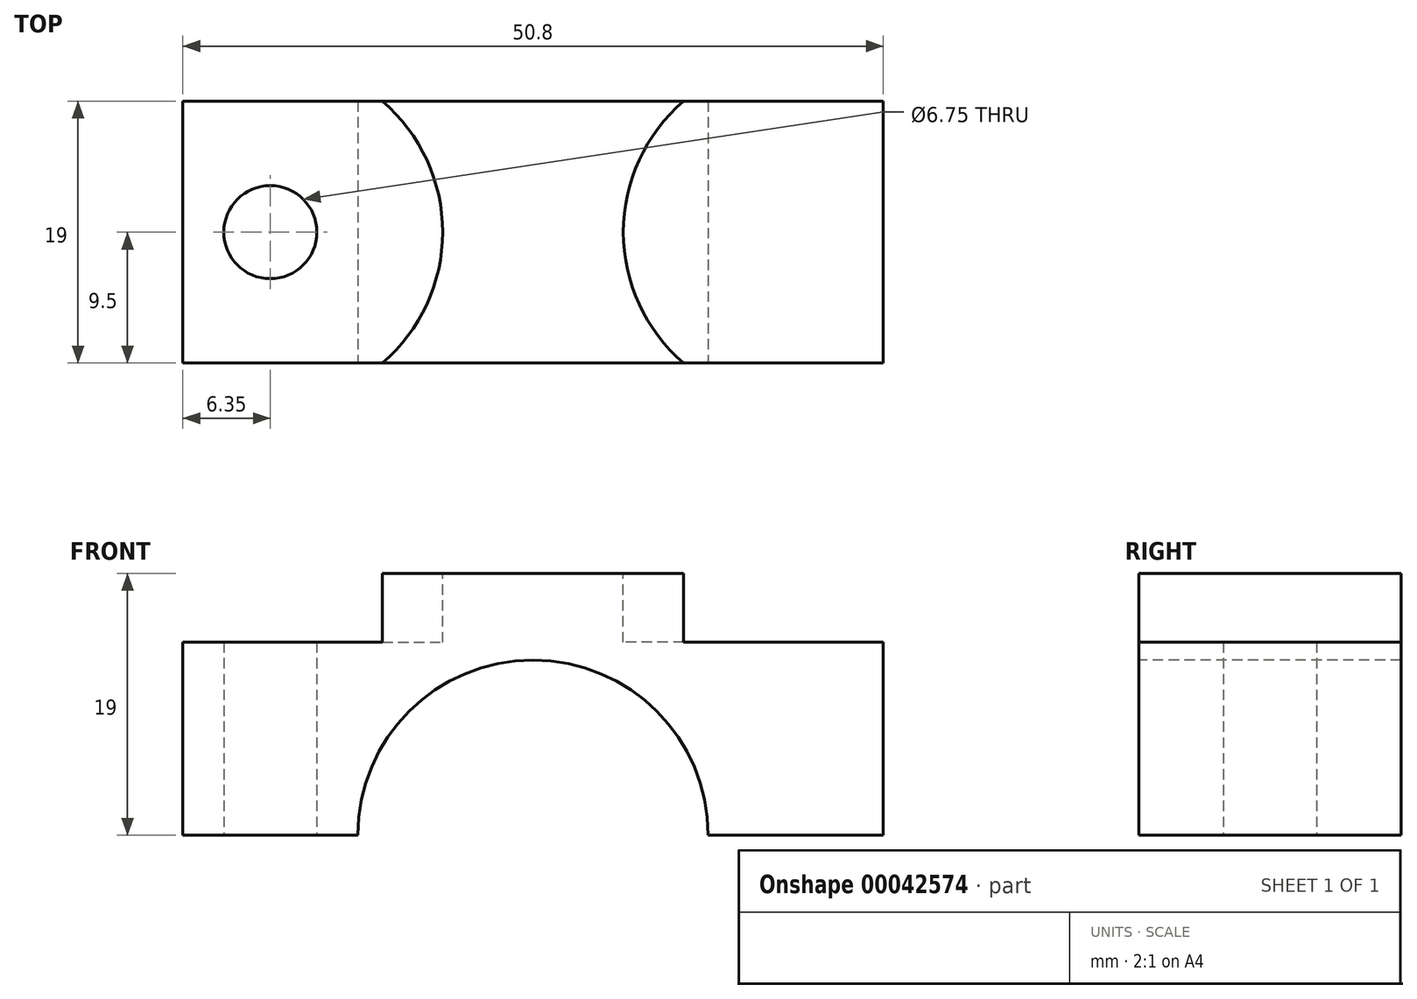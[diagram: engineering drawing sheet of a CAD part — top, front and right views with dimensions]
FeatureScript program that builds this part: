
annotation { "Feature Type Name" : "Feature", "Feature Type Description" : "" }
export const myFeature = defineFeature(function(context is Context, id is Id, definition is map)
    precondition{}
    {
        {
            var Q0;
            Q0=qCreatedBy(makeId("Front.planeOp"),FACE);
            var sketch = newSketch(context, id + "F0", { "sketchPlane" : qUnion([Q0])});
            skCircle(sketch, "E0", {"center": v(0, 0) * mm, "radius": 12.7 * mm});
            skLineSegment(sketch, "E1", {"start": v(0, 0) * mm, "end": v(25.4, 0) * mm});
            skLineSegment(sketch, "E2", {"start": v(25.4, 0) * mm, "end": v(25.4, 19) * mm});
            skLineSegment(sketch, "E3", {"start": v(25.4, 19) * mm, "end": v(-25.4, 19) * mm});
            skLineSegment(sketch, "E4", {"start": v(-25.4, 19) * mm, "end": v(-25.4, 0) * mm});
            skLineSegment(sketch, "E5", {"start": v(-25.4, 0) * mm, "end": v(0, 0) * mm});
            skSolve(sketch);
        }
        {
            var Q0;
            {var subQ6=sQuery(id+"F0.wireOp",EDGE,"E2");Q0=makeQuery(id+"F0.imprint","IMPRINT",FACE,{"disambiguationData":[TD([[makeQuery(id+"F0.imprint","IMPRINT",EDGE,{"derivedFrom":subQ6}),1.0]])]});}
            extrude(context, id + "F1", {"entities" : qUnion([Q0]), "oppositeDirection" : true, "depth" : 19 * mm});
        }
        {
            var Q0;
            Q0=makeQuery(id+"F1.opExtrude","SWEPT_FACE",FACE,{"disambiguationData":[OSD([sQuery(id+"F0.wireOp",EDGE,"E5")])]});
            var sketch = newSketch(context, id + "F2", { "sketchPlane" : qUnion([Q0])});
            skLineSegment(sketch, "E6", {"start": v(-19.05, 0) * mm, "end": v(-19.05, -9.5) * mm, "construction": true});
            skCircle(sketch, "E7", {"center": v(-19.05, -9.5) * mm, "radius": 3.38 * mm});
            skLineSegment(sketch, "E8", {"start": v(0, 10.43) * mm, "end": v(0, -35.36) * mm, "construction": true});
            skCircle(sketch, "E9.MirrorC", {"center": v(19.05, -9.5) * mm, "radius": 3.38 * mm});
            skSolve(sketch);
        }
        {
            var Q0;
            Q0=makeQuery(id+"F2.imprint","IMPRINT",FACE,{"disambiguationData":[TD([[makeQuery(id+"F2.imprint","IMPRINT",EDGE,{"derivedFrom":sQuery(id+"F2.wireOp",EDGE,"E7")}),1.0]])]});
            var Q1;
            Q1=makeQuery(id+"F2.imprint","IMPRINT",FACE,{"disambiguationData":[TD([[makeQuery(id+"F2.imprint","IMPRINT",EDGE,{"derivedFrom":sQuery(id+"F2.wireOp",EDGE,"E9.MirrorC")}),-1.0]])]});
            extrude(context, id + "F3", {"entities" : qUnion([Q0, Q1]), "operationType" : NewBodyOperationType.REMOVE, "endBound" : BoundingType.UP_TO_NEXT, "oppositeDirection" : true, "depth" : 25 * mm});
        }
        {
            var Q0;
            Q0=makeQuery(id+"F1.opExtrude","SWEPT_FACE",FACE,{"disambiguationData":[OSD([sQuery(id+"F0.wireOp",EDGE,"E3")])]});
            var sketch = newSketch(context, id + "F4", { "sketchPlane" : qUnion([Q0])});
            skCircle(sketch, "E10", {"center": v(-19.05, 9.5) * mm, "radius": 12.5 * mm});
            skCircle(sketch, "E11", {"center": v(19.05, 9.5) * mm, "radius": 12.5 * mm});
            skSolve(sketch);
        }
        {
            var Q0;
            Q0 = qSketchRegion(id + "F4", true);
            extrude(context, id + "F5", {"entities" : qUnion([Q0]), "operationType" : NewBodyOperationType.REMOVE, "oppositeDirection" : true, "depth" : 5 * mm});
        }
    });
